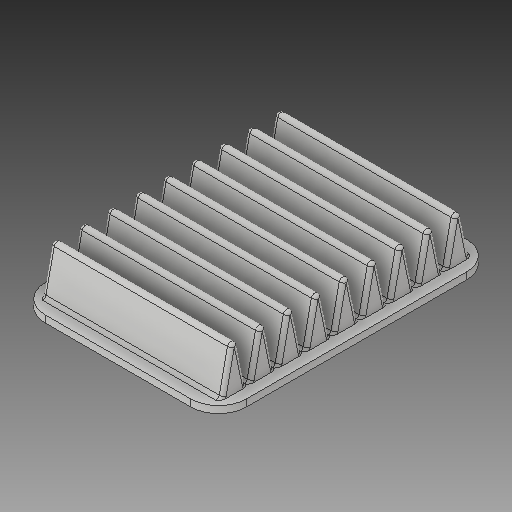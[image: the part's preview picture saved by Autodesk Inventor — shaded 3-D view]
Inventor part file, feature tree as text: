
AUTODESK INVENTOR PART (.ipt)
format: ipt  version: 2018 (Build 220112000, 112)  size: 323,584 bytes
history: native  units: in
note: dims shown in document units (in); Inventor stores cm internally (conversion verified against a paired STEP export)
features: extrude x2, fillet x2, sketch x2, pattern_linear x1
ambient origin geometry x8: Origin, YZ Plane, XZ Plane, XY Plane, X Axis, Y Axis, Z Axis, Center Point
bodies: Solid1 (feature_tree)
feature tree (7):
  extrude  "Extrusion1"  Depth=0.3937in
  fillet  "Fillet1"  Radius=0.3937in
  extrude  "Extrusion2"  Depth=0.125in
  fillet  "Fillet2"  Radius=2.2835in
  pattern_linear  "Rectangular Pattern1"  Spacing1=0.87in  [1 undecoded]
  sketch  "Sketch1"  dims[d0=9.8819in d1=7.2047in d2=0.3937in]
  sketch  "Sketch2"  dims[d3=0.25in d4=0.0in d5=1.0in d6=2.2835in d7=0.87in d8=6.45in d9=0.0in d10=0.125in d11=3.5433in d13=1.0in]
note: 1 required parameter value undecoded (feature->parameter linkage not recoverable at this tier; creation-order binding heuristic only, values carry confidence <= 0.55)
